# Revit family: NLRS_57_DUA_UN_connection-sleeve-for-bdhn-and-bdvn_LT_sacs
name_source: partatom
category: Duct Accessories
units: mm (PartAtom-declared; Revit-internal decimal feet)

## family parameters
Always vertical = Yes
Cut with Voids When Loaded = No
Part Type = Attaches To
Round Connector Dimension = Use Diameter
Shared = Yes
Work Plane-Based = No

## types (1)
- BDOKAD
    Assembly Code = 57.0
    Default Elevation = 200 mm  [stored 0.656168 ft]
    Description = Connection sleeve BDOKAD for BDHN/BDVN
    LookupTable = BDOKAD
    Manufacturer = Solid Air Climate Solutions
    Model = BDOKAD
    NLRS_C_content_datum_uitgifte = 25-07-2025
    NLRS_C_content_provider = Solid Air Climate Solutions
    NLRS_C_content_versie = 1.22.01
    NLRS_C_description = Connection sleeve BDOKAD for BDHN/BDVN
    SACS_Base_Index = 4
    SACS_Material = seawater proof aluminium

note: [stored X ft] marks values corroborated as IEEE doubles in the binary element streams (Revit-internal decimal feet)

## geometry (parser evidence)
native form markers: Sweep x7
no freeform markers — native parametric forms only
